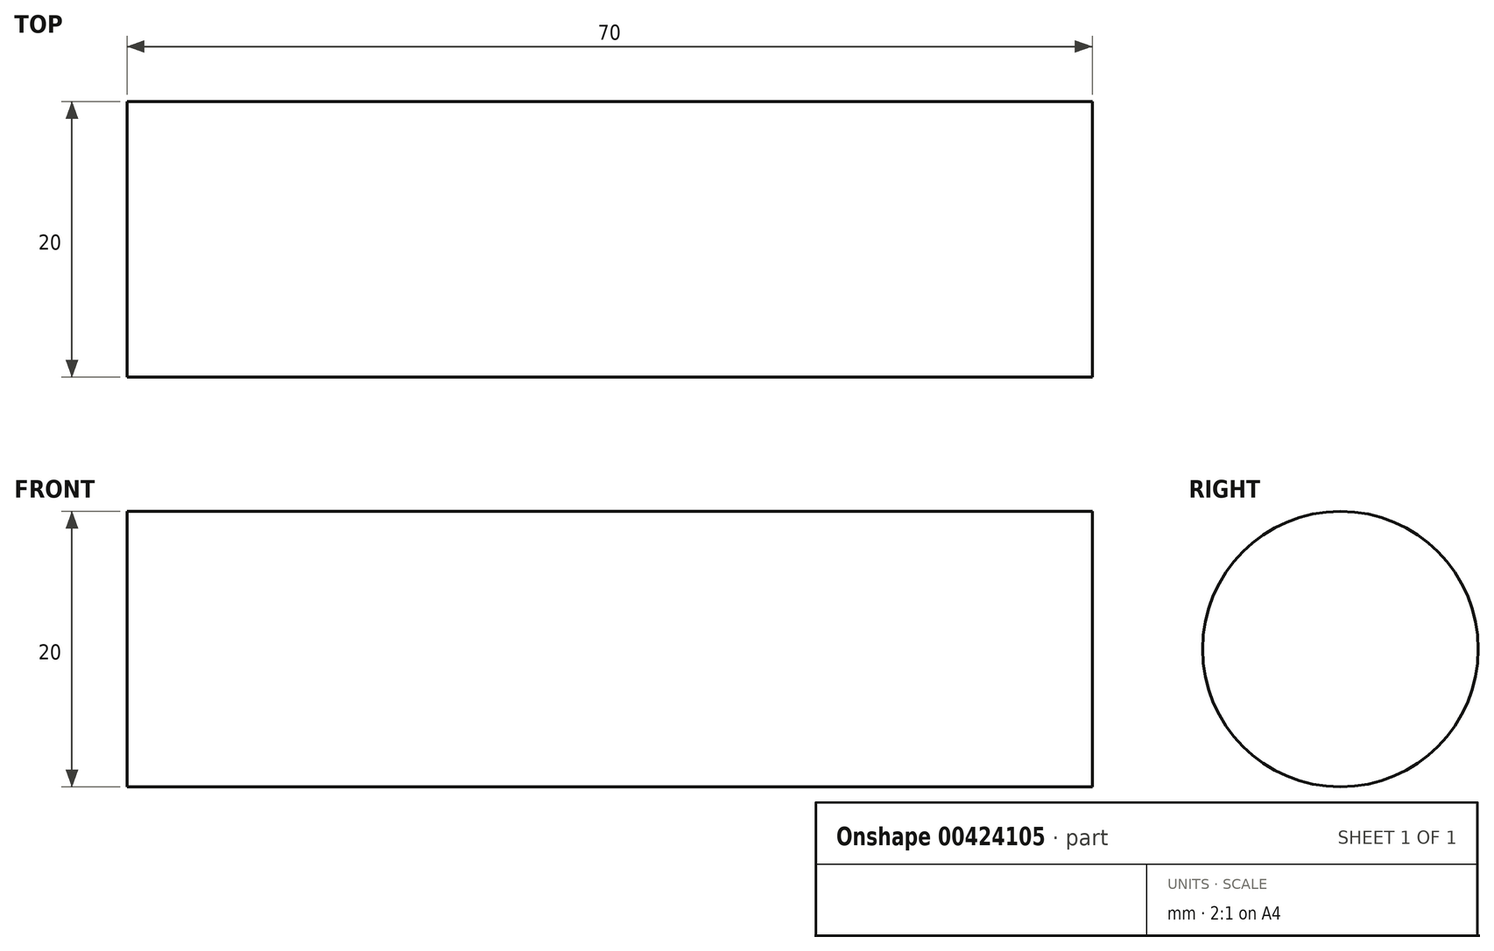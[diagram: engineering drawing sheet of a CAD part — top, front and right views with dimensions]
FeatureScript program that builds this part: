
annotation { "Feature Type Name" : "Feature", "Feature Type Description" : "" }
export const myFeature = defineFeature(function(context is Context, id is Id, definition is map)
    precondition{}
    {
        {
            var Q0;
            Q0=qCreatedBy(makeId("Right.planeOp"),FACE);
            var sketch = newSketch(context, id + "F0", { "sketchPlane" : qUnion([Q0])});
            skCircle(sketch, "E0", {"center": v(0, 0) * mm, "radius": 10 * mm});
            skSolve(sketch);
        }
        {
            var Q0;
            Q0=qSketchRegion(id+"F0",true);
            extrude(context, id + "F1", {"entities" : qUnion([Q0]), "depth" : 70 * mm});
        }
    });
